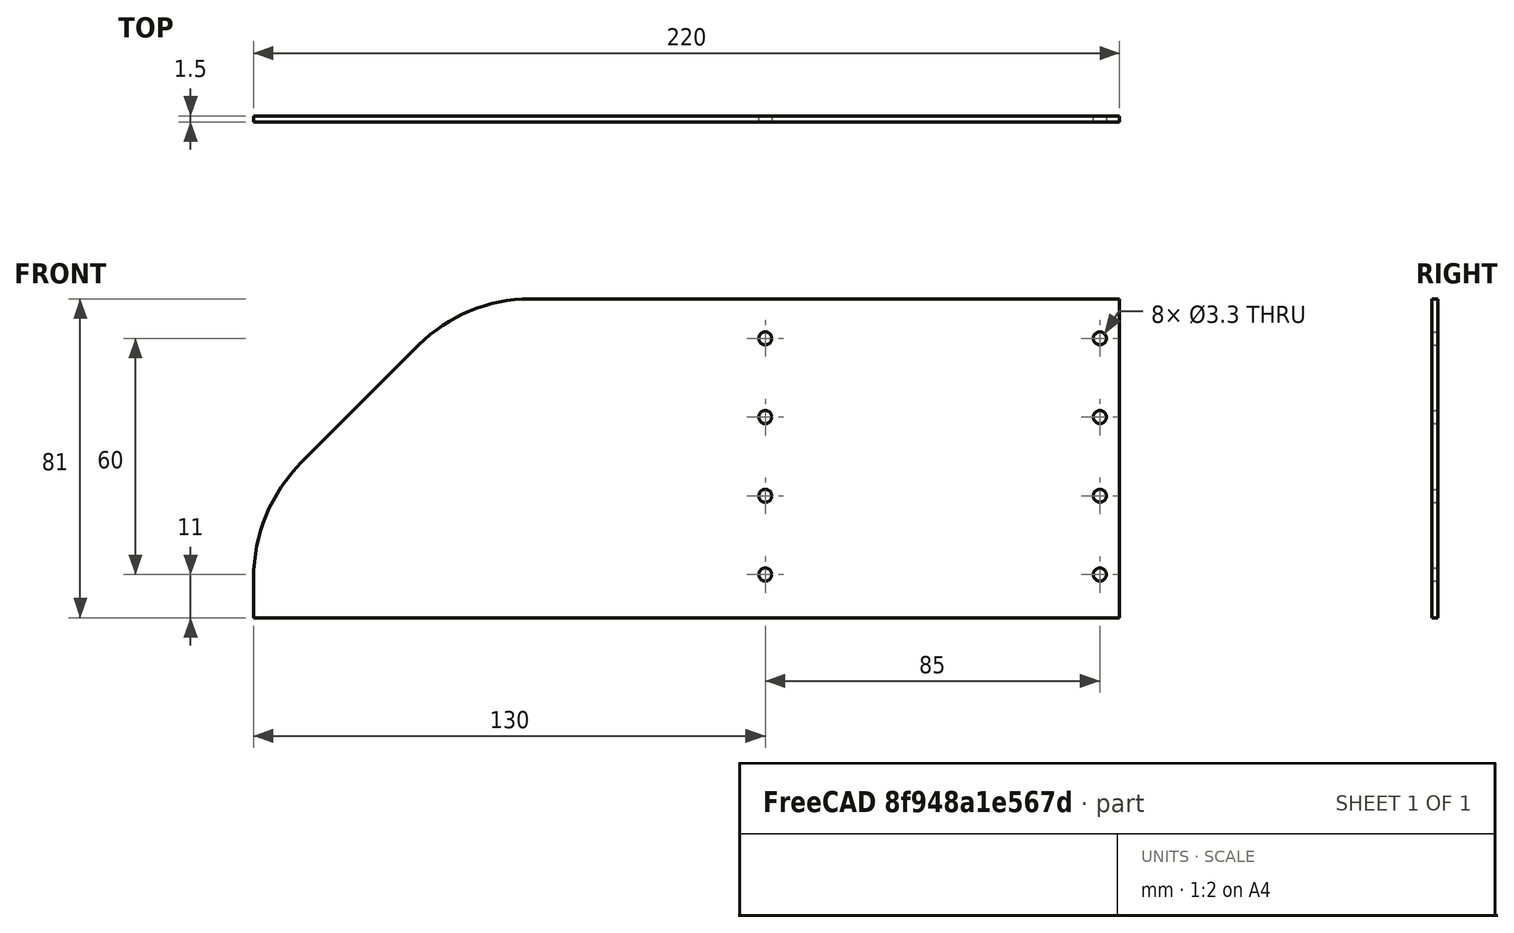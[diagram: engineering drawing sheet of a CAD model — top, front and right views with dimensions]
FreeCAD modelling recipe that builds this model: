
FCSTD DOCUMENT  (FreeCAD 1.0R39109 (Git))
Label: wall_screen
License: All rights reserved
LicenseURL: https://en.wikipedia.org/wiki/All_rights_reserved
objects: Sketcher::SketchObject×2, PartDesign::Pad×1, PartDesign::Body×1
note: 8 computed .brp shape members not serialized (recipe doc carries the construction recipe); baked Part::Feature solids carry a one-line shape summary decoded from their .brp

FEATURE [Sketcher::SketchObject] Sketch
  ArcFitTolerance = 1e-06
  AttachmentSupport = -> [XZ_Plane]
  FullyConstrained = true
  MakeInternals = false
  MapMode = 5
  Placement = pos=(0,0,0) rot=(1,0,0;1.5708rad)
  sketch-geometry (25):
    g0: LineSegment [constr] StartX=-110 StartY=41 StartZ=0 EndX=-110 EndY=-41 EndZ=0
    g1: LineSegment [constr] StartX=-110 StartY=-41 StartZ=0 EndX=110 EndY=-41 EndZ=0
    g2: LineSegment [constr] StartX=110 StartY=-41 StartZ=0 EndX=110 EndY=41 EndZ=0
    g3: LineSegment [constr] StartX=110 StartY=41 StartZ=0 EndX=-110 EndY=41 EndZ=0
    g4: GeomPoint [constr] X=0 Y=0 Z=0
    g5: LineSegment [constr] StartX=-110 StartY=40 StartZ=0 EndX=-110 EndY=-40 EndZ=0
    g6: LineSegment [constr] StartX=-110 StartY=-40 StartZ=0 EndX=110 EndY=-40 EndZ=0
    g7: LineSegment [constr] StartX=110 StartY=-40 StartZ=0 EndX=110 EndY=40 EndZ=0
    g8: LineSegment [constr] StartX=110 StartY=40 StartZ=0 EndX=-110 EndY=40 EndZ=0
    g9: GeomPoint [constr] X=0 Y=0 Z=0
    g10: LineSegment StartX=-110 StartY=-41 StartZ=0 EndX=-110 EndY=-31 EndZ=0
    g11: ArcOfCircle CenterX=-68.1594 CenterY=-31 CenterZ=0 NormalX=0 NormalY=0 NormalZ=1 AngleXU=0 Radius=41.8406 StartAngle=2.35619 EndAngle=3.14159
    g12: LineSegment StartX=-97.7452 StartY=-1.41421 StartZ=0 EndX=-68.0467 EndY=28.2843 EndZ=0
    g13: ArcOfCircle CenterX=-39.7624 CenterY=0 CenterZ=0 NormalX=0 NormalY=0 NormalZ=1 AngleXU=0 Radius=40 StartAngle=1.5708 EndAngle=2.35619
    g14: LineSegment StartX=-39.7624 StartY=40 StartZ=0 EndX=110 EndY=40 EndZ=0
    g15: LineSegment StartX=110 StartY=40 StartZ=0 EndX=110 EndY=-41 EndZ=0
    g16: LineSegment StartX=110 StartY=-41 StartZ=0 EndX=-110 EndY=-41 EndZ=0
    g17: Circle CenterX=105 CenterY=30 CenterZ=0 NormalX=0 NormalY=0 NormalZ=1 AngleXU=0 Radius=1.65
    g18: Circle CenterX=20 CenterY=30 CenterZ=0 NormalX=0 NormalY=0 NormalZ=1 AngleXU=0 Radius=1.65
    g19: Circle CenterX=20 CenterY=10 CenterZ=0 NormalX=0 NormalY=0 NormalZ=1 AngleXU=0 Radius=1.65
    g20: Circle CenterX=105 CenterY=10 CenterZ=0 NormalX=0 NormalY=0 NormalZ=1 AngleXU=0 Radius=1.65
    g21: Circle CenterX=105 CenterY=-30 CenterZ=0 NormalX=0 NormalY=0 NormalZ=1 AngleXU=0 Radius=1.65
    g22: Circle CenterX=20 CenterY=-30 CenterZ=0 NormalX=0 NormalY=0 NormalZ=1 AngleXU=0 Radius=1.65
    g23: Circle CenterX=20 CenterY=-10 CenterZ=0 NormalX=0 NormalY=0 NormalZ=1 AngleXU=0 Radius=1.65
    g24: Circle CenterX=105 CenterY=-10 CenterZ=0 NormalX=0 NormalY=0 NormalZ=1 AngleXU=0 Radius=1.65
  constraints (61):
    c: Coincident(g0,g1)
    c: Coincident(g1,g2)
    c: Coincident(g2,g3)
    c: Coincident(g3,g0)
    c: Vertical(g0)
    c: Vertical(g2)
    c: Horizontal(g1)
    c: Horizontal(g3)
    c: Symmetric(g2,g0,g4)
    c: Coincident(g4,g-1)
    c: DistanceX(g3,g3) = 220
    c: DistanceY(g2,g2) = 82
    c: Coincident(g5,g6)
    c: Coincident(g6,g7)
    c: Coincident(g7,g8)
    c: Coincident(g8,g5)
    c: Vertical(g5)
    c: Vertical(g7)
    c: Horizontal(g6)
    c: Horizontal(g8)
    c: Symmetric(g7,g5,g9)
    c: Coincident(g9,g4)
    c: PointOnObject(g6,g2)
    c: DistanceY(g1,g6) = 1
    c: Coincident(g0,g10)
    c: PointOnObject(g10,g0)
    c: Tangent(g10,g11) = 1.5708
    c: Tangent(g11,g12) = 1.5708
    c: Tangent(g12,g13) = 1.5708
    c: PointOnObject(g13,g8)
    c: Coincident(g14,g7)
    c: Coincident(g14,g15)
    c: Coincident(g15,g16)
    c: Coincident(g16,g10)
    c: Horizontal(g16)
    c: Tangent(g13,g14) = 1.5708
    c: Distance(g12) = 42
    c: Angle(g12) = 0.785398
    c: DistanceY(g10,g10) = 10
    c: Horizontal(g18,g17)
    c: DistanceX(g18,g17) = 85
    c: DistanceY(g17,g7) = 10
    c: DistanceX(g17,g7) = 5
    c: Equal(g18,g17)
    c: Radius(g18) = 1.65
    c: PointOnObject(g13,g-1)
    c: Vertical(g15)
    c: Vertical(g19,g18)
    c: Vertical(g20,g17)
    c: DistanceY(g20,g17) = 20
    c: Equal(g19,g18)
    c: Equal(g18,g20)
    c: Horizontal(g19,g20)
    c: Equal(g22,g21)
    c: Radius(g22) = 1.65
    c: Equal(g23,g22)
    c: Equal(g22,g24)
    c: Symmetric(g22,g18,g-1)
    c: Symmetric(g19,g23,g-1)
    c: Symmetric(g17,g21,g-1)
    c: Symmetric(g24,g20,g-1)
FEATURE [PartDesign::Pad] Pad  label="BasePad"
  Direction = (0,-1,2e-16)
  Length = 0.75
  Length2 = 0.75
  Placement = pos=(0,0,0) rot=(1,0,0;1.5708rad)
  Profile = -> Sketch
  ReferenceAxis = -> Sketch [N_Axis]
  Refine = true
  Suppressed = false
  Type = 4
FEATURE [Sketcher::SketchObject] Sketch001
  ArcFitTolerance = 1e-06
  AttachmentSupport = -> [Pad]
  ExternalGeometry = -> [Pad]
  FullyConstrained = true
  MakeInternals = false
  MapMode = 5
  Placement = pos=(0,-0.75,0) rot=(1,0,0;1.5708rad)
  sketch-geometry (1):
    g0: LineSegment StartX=110 StartY=40 StartZ=0 EndX=-5 EndY=40 EndZ=0
  constraints (7):
    c: Coincident(g0,g-7)
    c: PointOnObject(g0,g-7)
    c: DistanceX(g0,g0) = 115
    c: DistanceX(g-7,g0) = 34.7624
    c: Radius(g-6) = 40
    c: Radius(g-4) = 41.8406
    c: Distance(g-5) = 42
FEATURE [PartDesign::Body] Body  label="wall_screen"
  AllowCompound = false
  Group = -> [Sketch,Pad,Sketch001]
  Origin = -> Origin
  Tip = -> Pad
